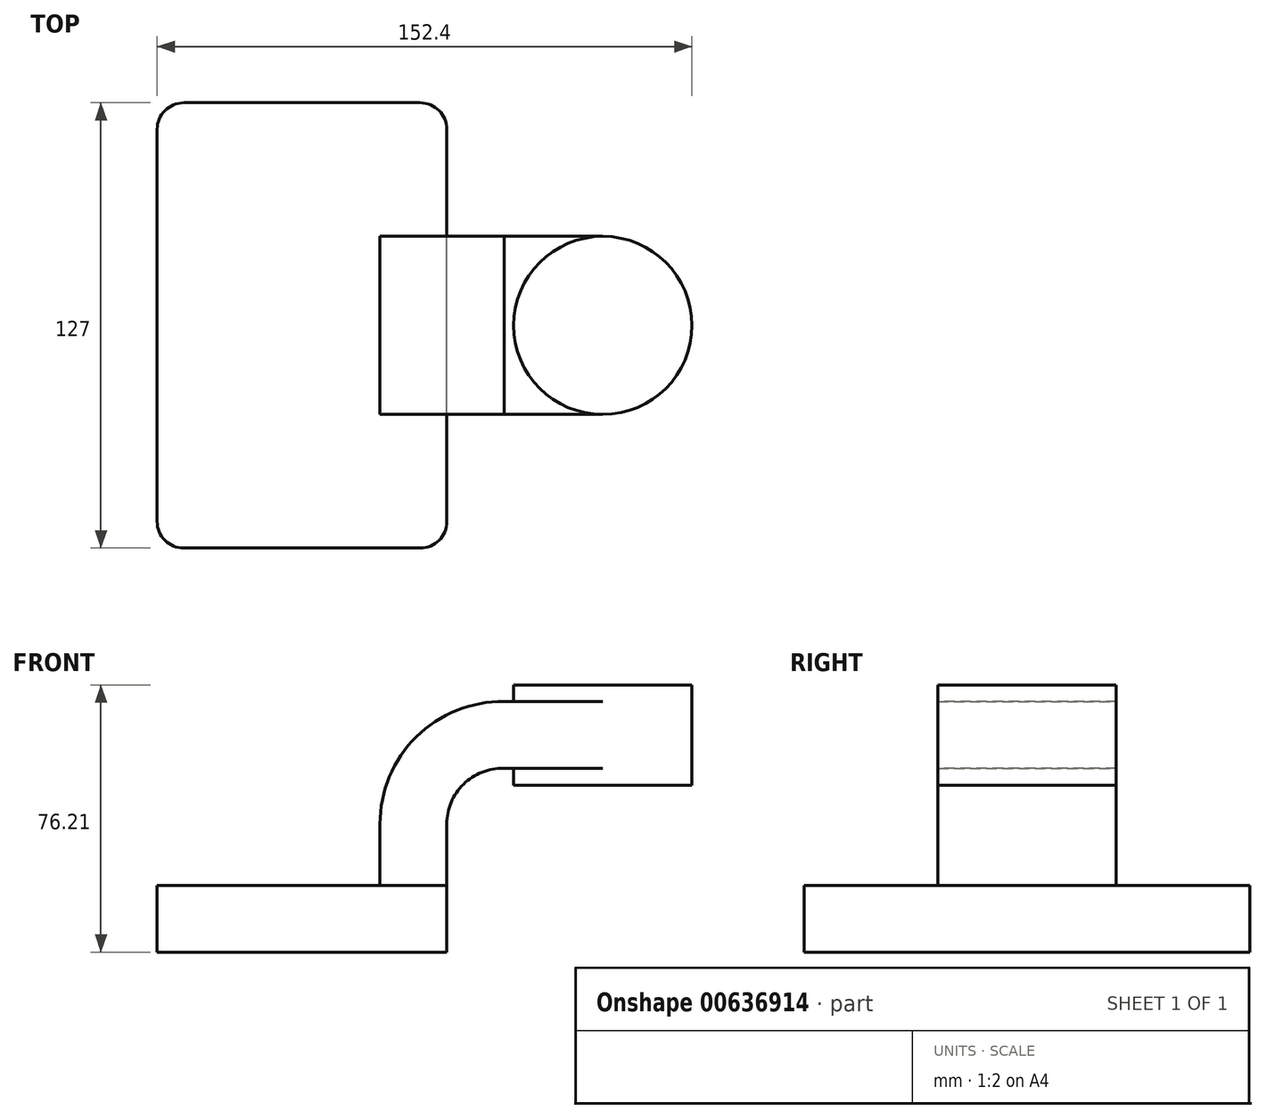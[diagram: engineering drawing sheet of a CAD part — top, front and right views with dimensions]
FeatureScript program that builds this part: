
annotation { "Feature Type Name" : "Feature", "Feature Type Description" : "" }
export const myFeature = defineFeature(function(context is Context, id is Id, definition is map)
    precondition{}
    {
        {
            var Q0;
            Q0=qCreatedBy(makeId("Front.planeOp"),FACE);
            var sketch = newSketch(context, id + "F0", { "sketchPlane" : qUnion([Q0])});
            skLineSegment(sketch, "E0.bottom", {"start": v(41.28, -9.52) * mm, "end": v(-41.27, -9.53) * mm});
            skLineSegment(sketch, "E0.top", {"start": v(41.28, 9.53) * mm, "end": v(-41.28, 9.53) * mm});
            skLineSegment(sketch, "E0.left", {"start": v(41.28, -9.52) * mm, "end": v(41.28, 9.53) * mm});
            skLineSegment(sketch, "E0.right", {"start": v(-41.28, -9.53) * mm, "end": v(-41.28, 9.53) * mm});
            skPoint(sketch, "E0.middle", {"position": v(0, 0) * mm});
            skLineSegment(sketch, "E1.bottom", {"start": v(60.33, 66.68) * mm, "end": v(111.12, 66.68) * mm});
            skLineSegment(sketch, "E1.top", {"start": v(60.33, 38.1) * mm, "end": v(111.12, 38.1) * mm});
            skLineSegment(sketch, "E1.left", {"start": v(60.33, 66.68) * mm, "end": v(60.33, 38.1) * mm});
            skLineSegment(sketch, "E1.right", {"start": v(111.12, 66.68) * mm, "end": v(111.12, 38.1) * mm});
            skPoint(sketch, "E1.middle", {"position": v(85.73, 52.39) * mm});
            skLineSegment(sketch, "E2", {"start": v(41.28, 9.53) * mm, "end": v(41.28, 27) * mm});
            skArc(sketch, "E3", {"start": v(41.28, 27) * mm, "mid": v(46.03, 38.33) * mm, "end": v(57.45, 42.88) * mm});
            skLineSegment(sketch, "E4", {"start": v(57.45, 42.88) * mm, "end": v(85.73, 42.88) * mm});
            skLineSegment(sketch, "E5.0", {"start": v(57.6, 61.93) * mm, "end": v(85.73, 61.93) * mm});
            skArc(sketch, "E5.1", {"start": v(22.23, 27) * mm, "mid": v(32.61, 51.86) * mm, "end": v(57.6, 61.93) * mm});
            skLineSegment(sketch, "E5.2", {"start": v(22.23, 9.53) * mm, "end": v(22.23, 27) * mm});
            skLineSegment(sketch, "E6", {"start": v(85.72, 66.68) * mm, "end": v(85.72, 38.1) * mm});
            skFitSpline(sketch, "E7", {"points": [v(-41.28, 9.52) * mm, v(57.6, 61.93) * mm], "startDerivative": vector(79.37, 106.82) * mm, "endDerivative": vector(123.6, -4.07) * mm});
            skSolve(sketch);
        }
        {
            var Q0;
            Q0=makeQuery(id+"F0.imprint","IMPRINT",FACE,{"disambiguationData":[TD([[makeQuery(id+"F0.imprint","IMPRINT",EDGE,{"derivedFrom":sQuery(id+"F0.wireOp",EDGE,"E0.bottom")}),-1.0]])]});
            extrude(context, id + "F1", {"entities" : qUnion([Q0]), "endBound" : BoundingType.SYMMETRIC, "depth" : 127 * mm, "offsetDistance" : 25.4 * mm});
        }
        {
            var Q0;
            {var subQ1=sQuery(id+"F0.wireOp",EDGE,"E2");Q0=makeQuery(id+"F0.imprint","IMPRINT",FACE,{"disambiguationData":[TD([[makeQuery(id+"F0.imprint","IMPRINT",EDGE,{"derivedFrom":subQ1}),1.0]])]});}
            var Q1;
            {var subQ0=sQuery(id+"F0.wireOp",EDGE,"E5.0");var subQ1=sQuery(id+"F0.wireOp",EDGE,"E1.left");var subQ2=makeQuery(id+"F0.imprint","INTERSECT",VERTEX,{"derivedFrom":[subQ1,subQ0]});Q1=makeQuery(id+"F0.imprint","IMPRINT",FACE,{"disambiguationData":[TD([[makeQuery(id+"F0.imprint","IMPRINT",EDGE,{"disambiguationData":[TD([[subQ2,-1.0]])],"derivedFrom":subQ1}),1.0]])]});}
            extrude(context, id + "F2", {"entities" : qUnion([Q0, Q1]), "endBound" : BoundingType.SYMMETRIC, "depth" : 50.8 * mm, "offsetDistance" : 25.4 * mm});
        }
        {
            var Q0;
            Q0=makeQuery(id+"F0.imprint","IMPRINT",FACE,{"disambiguationData":[TD([[makeQuery(id+"F0.imprint","IMPRINT",EDGE,{"derivedFrom":sQuery(id+"F0.wireOp",EDGE,"E5.1")}),1.0]])]});
            extrude(context, id + "F3", {"entities" : qUnion([Q0]), "endBound" : BoundingType.SYMMETRIC, "depth" : 15.88 * mm, "offsetDistance" : 25.4 * mm});
        }
        {
            var Q0;
            {var subQ0=sQuery(id+"F0.wireOp",EDGE,"E1.right");Q0=makeQuery(id+"F0.imprint","IMPRINT",FACE,{"disambiguationData":[TD([[makeQuery(id+"F0.imprint","IMPRINT",EDGE,{"derivedFrom":subQ0}),-1.0]])]});}
            var Q1;
            Q1=sQuery(id+"F0.wireOp",EDGE,"E6");
            revolve(context, id + "F4", {"operationType" : NewBodyOperationType.ADD, "entities" : qUnion([Q0]), "axis" : qUnion([Q1]), "revolveType" : RevolveType.FULL});
        }
        {
            var Q0;
            Q0=makeQuery(id+"F1.opExtrude","CAP_EDGE",EDGE,{"disambiguationData":[OSD([sQuery(id+"F0.wireOp",EDGE,"E0.right")])],"isStart":false});
            var Q1;
            Q1=makeQuery(id+"F1.opExtrude","CAP_EDGE",EDGE,{"disambiguationData":[OSD([sQuery(id+"F0.wireOp",EDGE,"E0.left")])],"isStart":false});
            var Q2;
            Q2=makeQuery(id+"F1.opExtrude","CAP_EDGE",EDGE,{"disambiguationData":[OSD([sQuery(id+"F0.wireOp",EDGE,"E0.left")])],"isStart":true});
            var Q3;
            Q3=makeQuery(id+"F1.opExtrude","CAP_EDGE",EDGE,{"disambiguationData":[OSD([sQuery(id+"F0.wireOp",EDGE,"E0.right")])],"isStart":true});
            fillet(context, id + "F5", {"entities" : qUnion([Q0, Q1, Q2, Q3]), "radius" : 7.62 * mm, "tangentPropagation" : true, "allowEdgeOverflow" : false});
        }
    });
